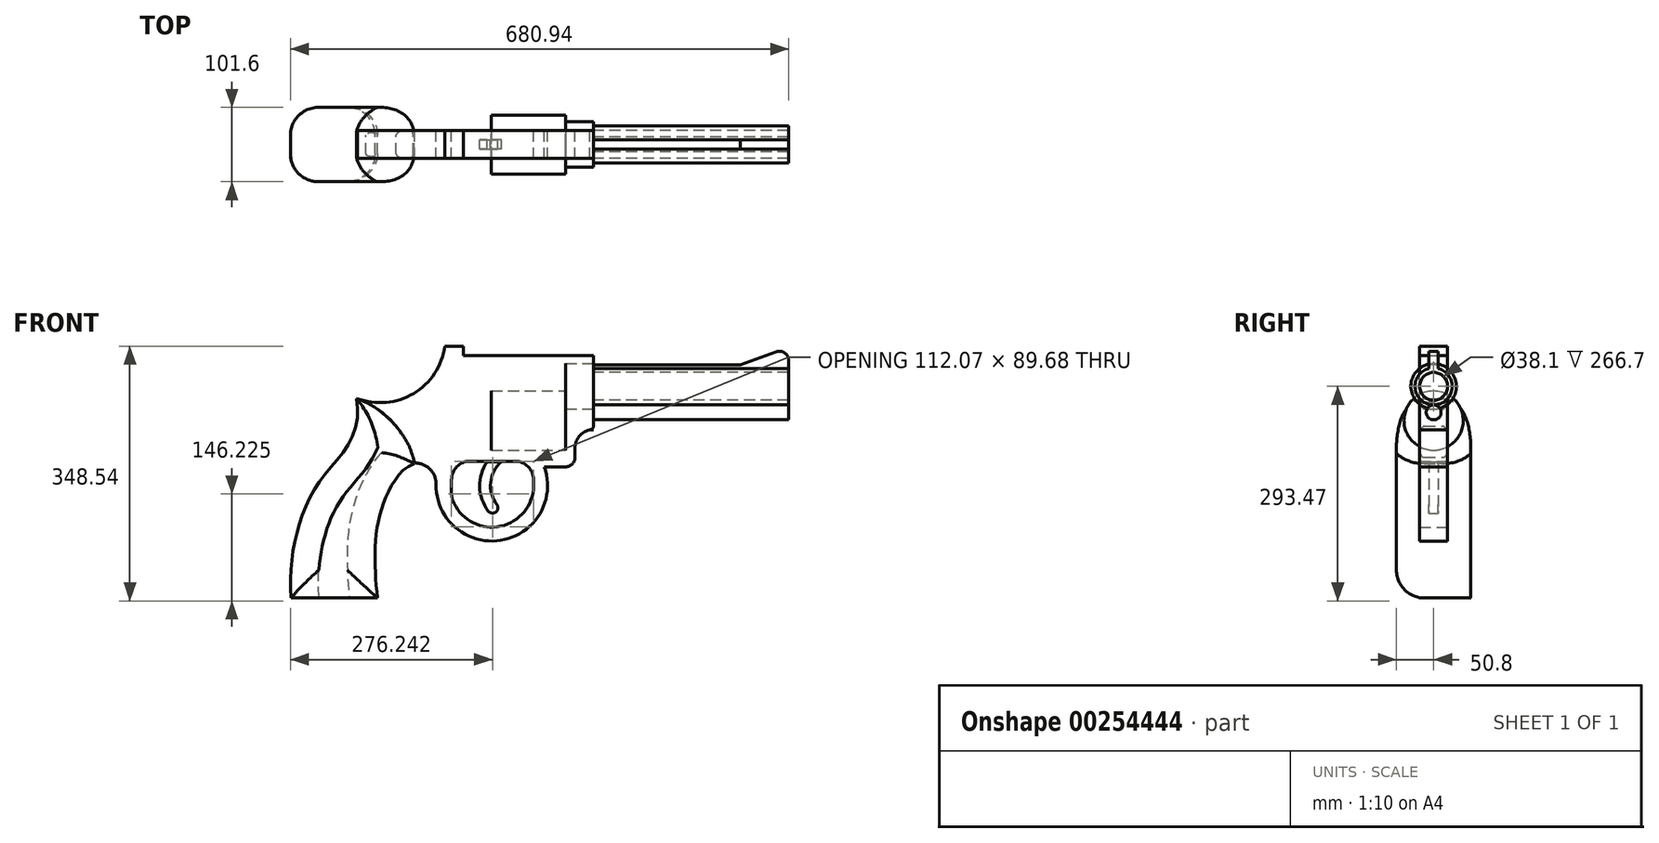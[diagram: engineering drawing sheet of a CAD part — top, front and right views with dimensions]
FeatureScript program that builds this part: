
annotation { "Feature Type Name" : "Feature", "Feature Type Description" : "" }
export const myFeature = defineFeature(function(context is Context, id is Id, definition is map)
    precondition{}
    {
        {
            var Q0;
            Q0=qCreatedBy(makeId("Right.planeOp"),FACE);
            var sketch = newSketch(context, id + "F0", { "sketchPlane" : qUnion([Q0])});
            skArc(sketch, "E0", {"start": v(-6.35, 265.9) * mm, "mid": v(0, 215.9) * mm, "end": v(6.35, 265.9) * mm});
            skCircle(sketch, "E1.0", {"center": v(0, 241.3) * mm, "radius": 19.05 * mm});
            skCircle(sketch, "E2", {"center": v(0, 205.74) * mm, "radius": 10.16 * mm});
            skLineSegment(sketch, "E3", {"start": v(-6.35, 265.9) * mm, "end": v(-6.35, 270.97) * mm});
            skLineSegment(sketch, "E4", {"start": v(-6.35, 270.97) * mm, "end": v(6.35, 270.97) * mm});
            skLineSegment(sketch, "E5", {"start": v(6.35, 270.97) * mm, "end": v(6.35, 265.9) * mm});
            skSolve(sketch);
        }
        {
            var Q0;
            Q0=makeQuery(id+"F0.imprint","IMPRINT",FACE,{"disambiguationData":[TD([[makeQuery(id+"F0.imprint","IMPRINT",EDGE,{"derivedFrom":sQuery(id+"F0.wireOp",EDGE,"E1.0")}),-1.0]])]});
            var Q1;
            Q1=makeQuery(id+"F0.imprint","IMPRINT",FACE,{"disambiguationData":[TD([[makeQuery(id+"F0.imprint","IMPRINT",EDGE,{"derivedFrom":sQuery(id+"F0.wireOp",EDGE,"E2")}),1.0]])]});
            extrude(context, id + "F1", {"entities" : qUnion([Q0, Q1]), "depth" : 215.9 * mm, "hasSecondDirection" : true, "secondDirectionOppositeDirection" : true, "secondDirectionDepth" : 50.8 * mm});
        }
        {
            var Q0;
            Q0=qCreatedBy(makeId("Front.planeOp"),FACE);
            var sketch = newSketch(context, id + "F2", { "sketchPlane" : qUnion([Q0])});
            skLineSegment(sketch, "E6", {"start": v(215.9, 270.97) * mm, "end": v(215.9, 276.75) * mm});
            skLineSegment(sketch, "E7", {"start": v(198.86, 288.68) * mm, "end": v(150.16, 270.97) * mm});
            skLineSegment(sketch, "E8", {"start": v(150.16, 270.97) * mm, "end": v(215.9, 270.97) * mm});
            skPoint(sketch, "E9.visualSharp", {"position": v(215.9, 294.88) * mm});
            skArc(sketch, "E9.filletArc", {"start": v(215.9, 276.75) * mm, "mid": v(210.49, 287.15) * mm, "end": v(198.86, 288.68) * mm});
            skSolve(sketch);
        }
        {
            var Q0;
            Q0 = qSketchRegion(id + "F2", true);
            extrude(context, id + "F3", {"entities" : qUnion([Q0]), "operationType" : NewBodyOperationType.ADD, "oppositeDirection" : true, "depth" : 6.35 * mm, "hasSecondDirection" : true, "secondDirectionOppositeDirection" : false, "secondDirectionDepth" : 6.35 * mm});
        }
        {
            var Q0;
            Q0=qCreatedBy(makeId("Front.planeOp"),FACE);
            var sketch = newSketch(context, id + "F4", { "sketchPlane" : qUnion([Q0])});
            skLineSegment(sketch, "E10", {"start": v(-50.8, 270.97) * mm, "end": v(-50.8, 187.15) * mm});
            skLineSegment(sketch, "E11", {"start": v(-50.8, 182.07) * mm, "end": v(-55.88, 182.07) * mm});
            skLineSegment(sketch, "E12", {"start": v(-76.2, 156.67) * mm, "end": v(-76.2, 143.97) * mm});
            skLineSegment(sketch, "E13", {"start": v(-88.9, 131.27) * mm, "end": v(-117.91, 131.27) * mm});
            skPoint(sketch, "E14.visualSharp", {"position": v(-50.8, 182.07) * mm});
            skArc(sketch, "E14.filletArc", {"start": v(-55.88, 182.07) * mm, "mid": v(-52.29, 183.56) * mm, "end": v(-50.8, 187.15) * mm});
            skPoint(sketch, "E15.visualSharp", {"position": v(-76.2, 182.07) * mm});
            skArc(sketch, "E15.filletArc", {"start": v(-50.8, 182.07) * mm, "mid": v(-68.76, 174.63) * mm, "end": v(-76.2, 156.67) * mm});
            skPoint(sketch, "E16.visualSharp", {"position": v(-76.2, 131.27) * mm});
            skArc(sketch, "E16.filletArc", {"start": v(-88.9, 131.27) * mm, "mid": v(-79.92, 135) * mm, "end": v(-76.2, 143.97) * mm});
            skArc(sketch, "E17", {"start": v(-265.94, 107.45) * mm, "mid": v(-178.49, 30.51) * mm, "end": v(-117.36, 129.67) * mm});
            skArc(sketch, "E18", {"start": v(-243.18, 85.59) * mm, "mid": v(-182.27, 49.22) * mm, "end": v(-132.89, 100.16) * mm});
            skArc(sketch, "E19", {"start": v(-265.94, 107.45) * mm, "mid": v(-274.3, 128.17) * mm, "end": v(-295.08, 136.4) * mm});
            skLineSegment(sketch, "E20.bottom", {"start": v(-242.81, 101.61) * mm, "end": v(-246.74, 101.61) * mm});
            skLineSegment(sketch, "E20.top", {"start": v(-158.16, 138.9) * mm, "end": v(-219.44, 138.9) * mm});
            skLineSegment(sketch, "E20.left", {"start": v(-132.76, 102.7) * mm, "end": v(-132.76, 113.5) * mm});
            skLineSegment(sketch, "E20.right", {"start": v(-244.84, 94.6) * mm, "end": v(-244.84, 113.5) * mm});
            skArc(sketch, "E21.filletArc", {"start": v(-219.44, 138.9) * mm, "mid": v(-237.4, 131.45) * mm, "end": v(-244.84, 113.5) * mm});
            skArc(sketch, "E22.filletArc", {"start": v(-132.76, 113.5) * mm, "mid": v(-140.2, 131.45) * mm, "end": v(-158.16, 138.9) * mm});
            skArc(sketch, "E23.trimOffspring", {"start": v(-265.94, 107.45) * mm, "mid": v(-177.65, 30.64) * mm, "end": v(-117.91, 131.27) * mm});
            skArc(sketch, "E24.filletArc", {"start": v(-244.84, 94.6) * mm, "mid": v(-244.42, 90.02) * mm, "end": v(-243.18, 85.59) * mm});
            skPoint(sketch, "E25.visualSharp", {"position": v(-132.76, 101.61) * mm});
            skArc(sketch, "E25.filletArc", {"start": v(-132.89, 100.16) * mm, "mid": v(-132.8, 101.43) * mm, "end": v(-132.76, 102.7) * mm});
            skArc(sketch, "E26", {"start": v(-295.08, 136.4) * mm, "mid": v(-323.42, 190.23) * mm, "end": v(-373.53, 224.7) * mm});
            skArc(sketch, "E27", {"start": v(-373.53, 224.7) * mm, "mid": v(-296.43, 231.64) * mm, "end": v(-254, 296.37) * mm});
            skLineSegment(sketch, "E28", {"start": v(-254, 296.37) * mm, "end": v(-228.6, 296.37) * mm});
            skLineSegment(sketch, "E29", {"start": v(-228.6, 296.37) * mm, "end": v(-228.6, 283.67) * mm});
            skLineSegment(sketch, "E30", {"start": v(-228.6, 283.67) * mm, "end": v(-50.8, 283.67) * mm});
            skLineSegment(sketch, "E31", {"start": v(-50.8, 283.67) * mm, "end": v(-50.8, 270.97) * mm});
            skSolve(sketch);
        }
        {
            var Q0;
            Q0 = qSketchRegion(id + "F4", true);
            var Q1;
            Q1=makeQuery(id+"F4.imprint","IMPRINT",FACE,{"disambiguationData":[TD([[makeQuery(id+"F4.imprint","IMPRINT",EDGE,{"derivedFrom":sQuery(id+"F4.wireOp",EDGE,"E10")}),-1.0]])]});
            extrude(context, id + "F5", {"entities" : qUnion([Q0, Q1]), "depth" : 19.05 * mm, "hasSecondDirection" : true, "secondDirectionOppositeDirection" : true, "secondDirectionDepth" : 19.05 * mm});
        }
        {
            var Q0;
            Q0=qCreatedBy(makeId("Front.planeOp"),FACE);
            var sketch = newSketch(context, id + "F6", { "sketchPlane" : qUnion([Q0])});
            skArc(sketch, "E32", {"start": v(-176.64, 138.15) * mm, "mid": v(-191.33, 110.15) * mm, "end": v(-182.84, 79.7) * mm});
            skArc(sketch, "E33", {"start": v(-196.32, 138.15) * mm, "mid": v(-206.34, 104.18) * mm, "end": v(-194.61, 70.75) * mm});
            skArc(sketch, "E34", {"start": v(-194.61, 70.75) * mm, "mid": v(-184.25, 69.34) * mm, "end": v(-182.84, 79.7) * mm});
            skLineSegment(sketch, "E35", {"start": v(-176.64, 138.15) * mm, "end": v(-196.32, 138.15) * mm});
            skSolve(sketch);
        }
        {
            var Q0;
            Q0 = qSketchRegion(id + "F6", true);
            extrude(context, id + "F7", {"entities" : qUnion([Q0]), "depth" : 6.35 * mm, "hasSecondDirection" : true, "secondDirectionOppositeDirection" : true, "secondDirectionDepth" : 6.35 * mm});
        }
        {
            var Q0;
            Q0=qCreatedBy(makeId("Right.planeOp"),FACE);
            var sketch = newSketch(context, id + "F8", { "sketchPlane" : qUnion([Q0])});
            skCircle(sketch, "E36", {"center": v(0, 241.31) * mm, "radius": 31.06 * mm});
            skSolve(sketch);
        }
        {
            var Q0;
            Q0 = qSketchRegion(id + "F8", true);
            extrude(context, id + "F9", {"entities" : qUnion([Q0]), "oppositeDirection" : true, "depth" : 38.1 * mm});
        }
        {
            var Q0;
            Q0=makeQuery(id+"F9.opExtrude","SWEPT_BODY",BODY,{"disambiguationData":[OSD([sQuery(id+"F8.wireOp",EDGE,"E36")])]});
            var Q1;
            Q1=qCreatedBy(makeId("Right.planeOp"),FACE);
            transform(context, id + "F10", {"entities" : qUnion([Q0]), "transformType" : TransformType.TRANSLATION_DISTANCE, "transformDirection" : qUnion([Q1]), "distance" : 50.8 * mm, "oppositeDirection" : true, "makeCopy" : false});
        }
        {
            var Q0;
            Q0=qCreatedBy(makeId("Right.planeOp"),FACE);
            var sketch = newSketch(context, id + "F11", { "sketchPlane" : qUnion([Q0])});
            skCircle(sketch, "E37", {"center": v(0, 194.45) * mm, "radius": 40.5 * mm});
            skSolve(sketch);
        }
        {
            var Q0;
            Q0=makeQuery(id+"F11.imprint","IMPRINT",FACE,{"disambiguationData":[TD([[makeQuery(id+"F11.imprint","IMPRINT",EDGE,{"derivedFrom":sQuery(id+"F11.wireOp",EDGE,"E37")}),1.0]])]});
            extrude(context, id + "F12", {"entities" : qUnion([Q0]), "oppositeDirection" : true, "depth" : 101.6 * mm});
        }
        {
            var Q0;
            Q0=makeQuery(id+"F12.opExtrude","SWEPT_BODY",BODY,{"disambiguationData":[OSD([sQuery(id+"F11.wireOp",EDGE,"E37")])]});
            var Q1;
            Q1=qCreatedBy(makeId("Right.planeOp"),FACE);
            transform(context, id + "F13", {"entities" : qUnion([Q0]), "transformType" : TransformType.TRANSLATION_DISTANCE, "transformDirection" : qUnion([Q1]), "distance" : 88.9 * mm, "oppositeDirection" : true, "makeCopy" : false});
        }
        {
            var Q0;
            Q0=qCreatedBy(makeId("Right.planeOp"),FACE);
            var sketch = newSketch(context, id + "F14", { "sketchPlane" : qUnion([Q0])});
            skLineSegment(sketch, "E38", {"start": v(0, 248.2) * mm, "end": v(0, 140.16) * mm, "construction": true});
            skArc(sketch, "E39", {"start": v(0, 153.18) * mm, "mid": v(40.47, 193.65) * mm, "end": v(0, 234.12) * mm});
            skPoint(sketch, "E40.orphan", {"position": v(0, 231.17) * mm});
            skPoint(sketch, "E41.orphan", {"position": v(0, 156.13) * mm});
            skSolve(sketch);
        }
        {
            var Q0;
            Q0 = qSketchRegion(id + "F14", true);
            var Q1;
            Q1=sQuery(id+"F14.wireOp",EDGE,"E39");
            var Q2;
            Q2=sQuery(id+"F14.wireOp",EDGE,"E38");
            revolve(context, id + "F15", {"bodyType" : ToolBodyType.SURFACE, "entities" : qUnion([Q0]), "surfaceEntities" : qUnion([Q1]), "axis" : qUnion([Q2]), "revolveType" : RevolveType.ONE_DIRECTION, "oppositeDirection" : true, "angle" : 180 * degree});
        }
        {
            var Q0;
            Q0=makeQuery(id+"F15.opRevolve","SWEPT_BODY",BODY,{"disambiguationData":[OSD([sQuery(id+"F14.wireOp",EDGE,"E39")])]});
            var Q1;
            Q1=qCreatedBy(makeId("Right.planeOp"),FACE);
            transform(context, id + "F16", {"entities" : qUnion([Q0]), "transformType" : TransformType.TRANSLATION_DISTANCE, "transformDirection" : qUnion([Q1]), "distance" : 203.2 * mm, "oppositeDirection" : true, "makeCopy" : false});
        }
        {
            var Q0;
            Q0=makeQuery(id+"F15.opRevolve","SWEPT_BODY",BODY,{"disambiguationData":[OSD([sQuery(id+"F14.wireOp",EDGE,"E39")])]});
            var Q1;
            Q1=qCreatedBy(makeId("Right.planeOp"),FACE);
            transform(context, id + "F17", {"entities" : qUnion([Q0]), "transformType" : TransformType.TRANSLATION_DISTANCE, "transformDirection" : qUnion([Q1]), "distance" : 12.7 * mm, "makeCopy" : false});
        }
        {
            var Q0;
            Q0=makeQuery(id+"F15.opRevolve","SWEPT_BODY",BODY,{"disambiguationData":[OSD([sQuery(id+"F14.wireOp",EDGE,"E39")])]});
            var Q1;
            Q1=qCreatedBy(makeId("Right.planeOp"),FACE);
            transform(context, id + "F18", {"entities" : qUnion([Q0]), "transformType" : TransformType.TRANSLATION_DISTANCE, "transformDirection" : qUnion([Q1]), "distance" : 6.35 * mm, "oppositeDirection" : true, "makeCopy" : false});
        }
        {
            var Q0;
            Q0=qCreatedBy(makeId("Front.planeOp"),FACE);
            var sketch = newSketch(context, id + "F19", { "sketchPlane" : qUnion([Q0])});
            skFitSpline(sketch, "E42", {"points": [v(-295.97, 135.37) * mm, v(-315.66, 121.53) * mm, v(-342.8, 65.11) * mm, v(-349.2, 0) * mm, v(-346, -48.26) * mm], "startDerivative": vector(-116.91, -52.78) * mm, "endDerivative": vector(18.49, -146.52) * mm});
            skFitSpline(sketch, "E43", {"points": [v(-374.74, 224.25) * mm, v(-374.21, 193.38) * mm, v(-388.05, 158.26) * mm, v(-413.74, 126.05) * mm, v(-448.96, 64.85) * mm, v(-463.97, -47.74) * mm], "startDerivative": vector(25.4, -198.34) * mm, "endDerivative": vector(39.5, -350.92) * mm});
            skLineSegment(sketch, "E44", {"start": v(-463.97, -47.74) * mm, "end": v(-346, -48.26) * mm});
            skFitSpline(sketch, "E45", {"points": [v(-374.74, 224.25) * mm, v(-332.33, 198.8) * mm, v(-295.97, 135.37) * mm], "startDerivative": vector(113.06, -31.02) * mm, "endDerivative": vector(12.54, -151.1) * mm});
            skSolve(sketch);
        }
        {
            var Q0;
            Q0=makeQuery(id+"F19.imprint","IMPRINT",FACE,{"disambiguationData":[TD([[makeQuery(id+"F19.imprint","IMPRINT",EDGE,{"derivedFrom":sQuery(id+"F19.wireOp",EDGE,"E42")}),-1.0]])]});
            extrude(context, id + "F20", {"entities" : qUnion([Q0]), "operationType" : NewBodyOperationType.ADD, "depth" : 50.8 * mm, "hasSecondDirection" : true, "secondDirectionOppositeDirection" : true, "secondDirectionDepth" : 50.8 * mm});
        }
        {
            var Q0;
            Q0=makeQuery(id+"F20.opExtrude","CAP_EDGE",EDGE,{"disambiguationData":[OSD([sQuery(id+"F19.wireOp",EDGE,"E43")])],"isStart":true});
            var Q1;
            Q1=makeQuery(id+"F20.opExtrude","CAP_EDGE",EDGE,{"disambiguationData":[OSD([sQuery(id+"F19.wireOp",EDGE,"E45")])],"isStart":true});
            var Q2;
            Q2=makeQuery(id+"F20.opExtrude","CAP_EDGE",EDGE,{"disambiguationData":[OSD([sQuery(id+"F19.wireOp",EDGE,"E42")])],"isStart":true});
            var Q3;
            Q3=makeQuery(id+"F20.opExtrude","CAP_EDGE",EDGE,{"disambiguationData":[OSD([sQuery(id+"F19.wireOp",EDGE,"E43")])],"isStart":false});
            var Q4;
            Q4=makeQuery(id+"F20.opExtrude","CAP_FACE",FACE,{"disambiguationData":[OSD([sQuery(id+"F19.wireOp",EDGE,"E42"),sQuery(id+"F19.wireOp",EDGE,"E43"),sQuery(id+"F19.wireOp",EDGE,"E44"),sQuery(id+"F19.wireOp",EDGE,"E45")])],"isStart":false});
            var Q5;
            Q5=makeQuery(id+"F20.opExtrude","CAP_EDGE",EDGE,{"disambiguationData":[OSD([sQuery(id+"F19.wireOp",EDGE,"E42")])],"isStart":false});
            fillet(context, id + "F21", {"entities" : qUnion([Q0, Q1, Q2, Q3, Q4, Q5]), "radius" : 38.1 * mm, "tangentPropagation" : true, "allowEdgeOverflow" : false});
        }
    });
